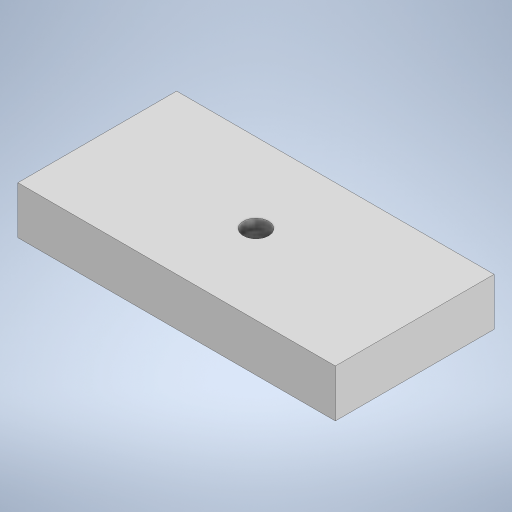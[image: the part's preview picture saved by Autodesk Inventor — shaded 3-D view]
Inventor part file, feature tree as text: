
AUTODESK INVENTOR PART (.ipt)
format: ipt  version: 2024 (Build 280153000, 153)  size: 201,216 bytes
history: native  units: mm
features: sketch x2, other x1, extrude x1, hole x1
ambient origin geometry x8: Origin, YZ Plane, XZ Plane, XY Plane, X Axis, Y Axis, Z Axis, Center Point
bodies: Body1 (feature_tree)
feature tree (5):
  other  "Bryła1"
  extrude  "Wyciągnięcie proste1"  Depth=200.0mm
  hole  "Otwór1"  [1 undecoded]
  sketch  "Szkic1"
  sketch  "Szkic2"
note: 1 required parameter value undecoded (feature->parameter linkage not recoverable at this tier; creation-order binding heuristic only, values carry confidence <= 0.55)
